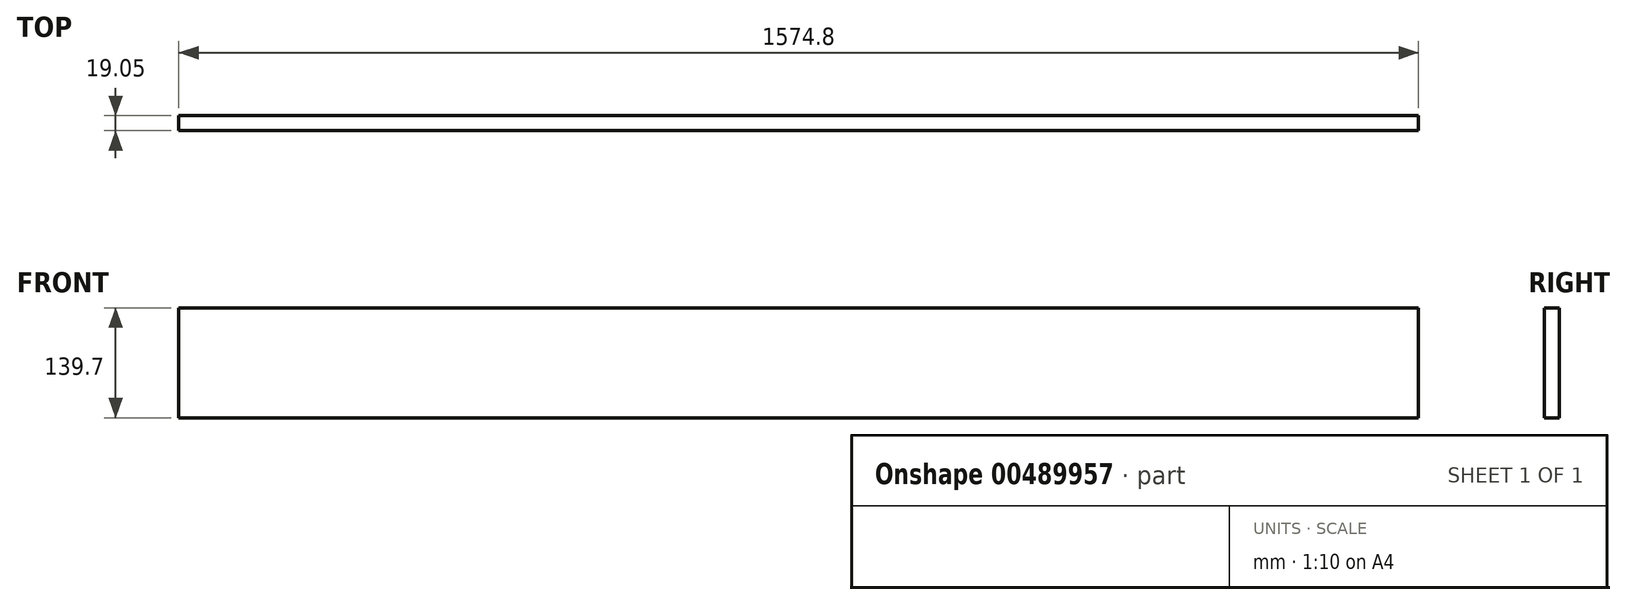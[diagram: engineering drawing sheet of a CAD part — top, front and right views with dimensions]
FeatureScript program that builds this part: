
annotation { "Feature Type Name" : "Feature", "Feature Type Description" : "" }
export const myFeature = defineFeature(function(context is Context, id is Id, definition is map)
    precondition{}
    {
        {
            var Q0;
            Q0=qCreatedBy(makeId("Front.planeOp"),FACE);
            var sketch = newSketch(context, id + "F0", { "sketchPlane" : qUnion([Q0])});
            skLineSegment(sketch, "E0.bottom", {"start": v(-787.4, -69.85) * mm, "end": v(787.4, -69.85) * mm});
            skLineSegment(sketch, "E0.top", {"start": v(-787.4, 69.85) * mm, "end": v(787.4, 69.85) * mm});
            skLineSegment(sketch, "E0.left", {"start": v(-787.4, -69.85) * mm, "end": v(-787.4, 69.85) * mm});
            skLineSegment(sketch, "E0.right", {"start": v(787.4, -69.85) * mm, "end": v(787.4, 69.85) * mm});
            skPoint(sketch, "E0.middle", {"position": v(0, 0) * mm});
            skSolve(sketch);
        }
        {
            var Q0;
            Q0 = qSketchRegion(id + "F0", true);
            extrude(context, id + "F1", {"entities" : qUnion([Q0]), "depth" : 19.05 * mm});
        }
    });
